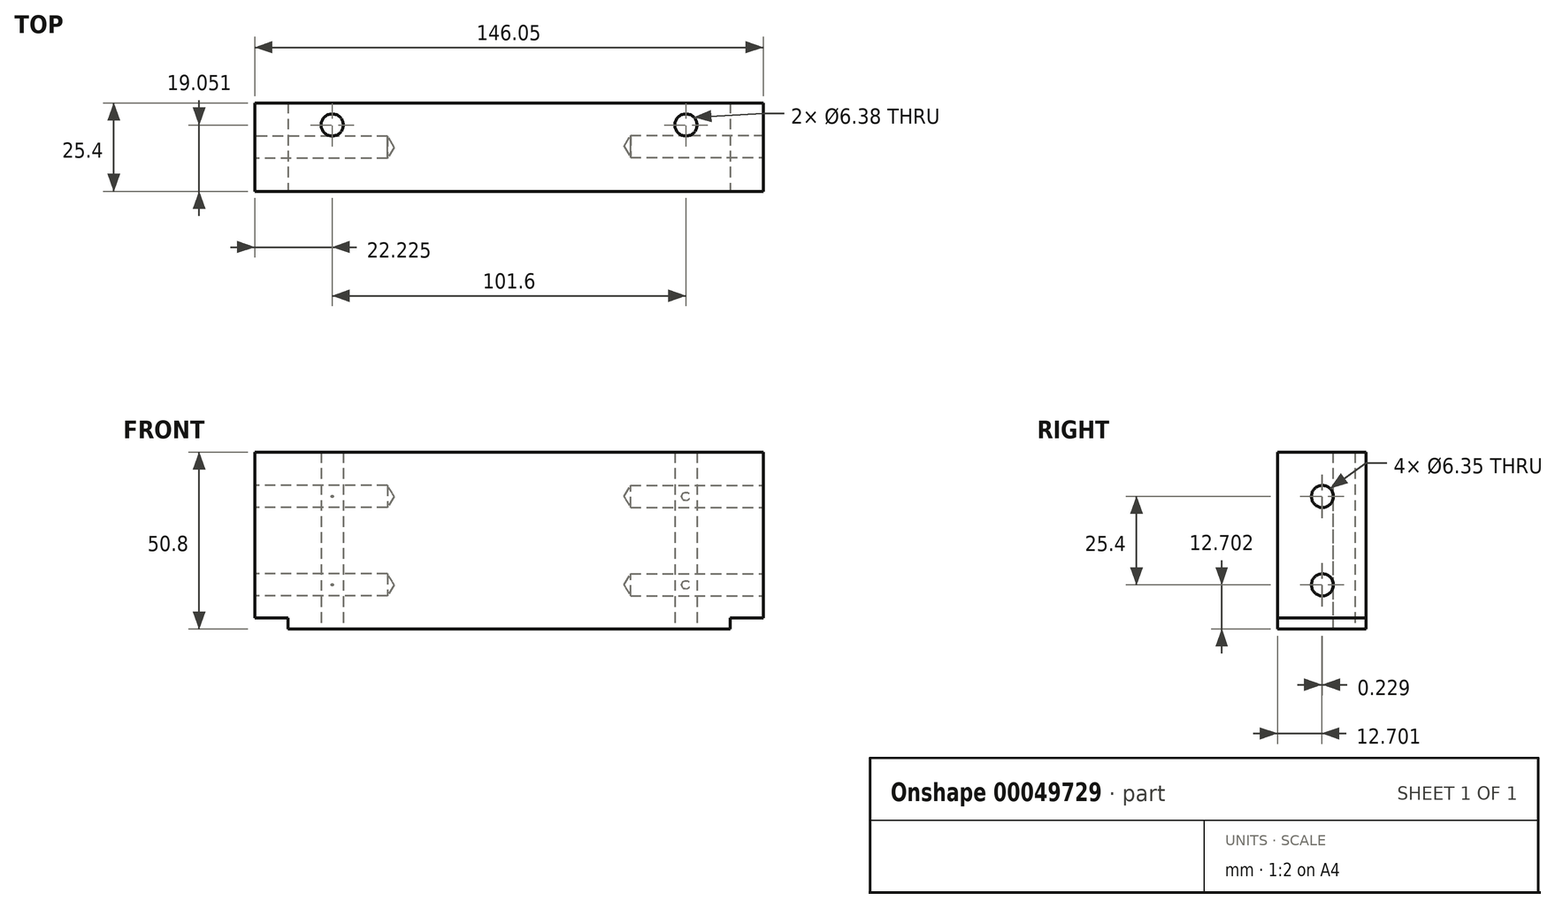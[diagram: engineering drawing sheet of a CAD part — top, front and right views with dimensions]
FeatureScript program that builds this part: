
annotation { "Feature Type Name" : "Feature", "Feature Type Description" : "" }
export const myFeature = defineFeature(function(context is Context, id is Id, definition is map)
    precondition{}
    {
        {
            var Q0;
            Q0=qCreatedBy(makeId("Right.planeOp"),FACE);
            var sketch = newSketch(context, id + "F0", { "sketchPlane" : qUnion([Q0])});
            skLineSegment(sketch, "E0.bottom", {"start": v(-12.93, 36.02) * mm, "end": v(12.47, 36.02) * mm});
            skLineSegment(sketch, "E0.top", {"start": v(-12.93, -14.78) * mm, "end": v(12.47, -14.78) * mm});
            skLineSegment(sketch, "E0.left", {"start": v(-12.93, 36.02) * mm, "end": v(-12.93, -14.78) * mm});
            skLineSegment(sketch, "E0.right", {"start": v(12.47, 36.02) * mm, "end": v(12.47, -14.78) * mm});
            skSolve(sketch);
        }
        {
            var Q0;
            Q0 = qSketchRegion(id + "F0", true);
            extrude(context, id + "F1", {"entities" : qUnion([Q0]), "depth" : 146.05 * mm});
        }
        {
            var Q0;
            Q0=makeQuery(id+"F1.opExtrude","SWEPT_FACE",FACE,{"disambiguationData":[OSD([sQuery(id+"F0.wireOp",EDGE,"E0.top")])]});
            var sketch = newSketch(context, id + "F2", { "sketchPlane" : qUnion([Q0])});
            skLineSegment(sketch, "E1.bottom", {"start": v(146.05, -12.47) * mm, "end": v(136.53, -12.47) * mm});
            skLineSegment(sketch, "E1.top", {"start": v(146.05, 12.93) * mm, "end": v(136.53, 12.93) * mm});
            skLineSegment(sketch, "E1.left", {"start": v(146.05, -12.47) * mm, "end": v(146.05, 12.93) * mm});
            skLineSegment(sketch, "E1.right", {"start": v(136.53, -12.47) * mm, "end": v(136.53, 12.93) * mm});
            skLineSegment(sketch, "E2.bottom", {"start": v(0, -12.47) * mm, "end": v(9.53, -12.47) * mm});
            skLineSegment(sketch, "E2.top", {"start": v(0, 12.93) * mm, "end": v(9.52, 12.93) * mm});
            skLineSegment(sketch, "E2.left", {"start": v(0, -12.47) * mm, "end": v(0, 12.93) * mm});
            skLineSegment(sketch, "E2.right", {"start": v(9.53, -12.47) * mm, "end": v(9.52, 12.93) * mm});
            skSolve(sketch);
        }
        {
            var Q0;
            Q0 = qSketchRegion(id + "F2", true);
            extrude(context, id + "F3", {"entities" : qUnion([Q0]), "operationType" : NewBodyOperationType.REMOVE, "oppositeDirection" : true, "depth" : 3.17 * mm});
        }
        {
            var Q0;
            Q0=makeQuery(id+"F1.opExtrude","CAP_FACE",FACE,{"disambiguationData":[OSD([sQuery(id+"F0.wireOp",EDGE,"E0.bottom"),sQuery(id+"F0.wireOp",EDGE,"E0.top"),sQuery(id+"F0.wireOp",EDGE,"E0.left"),sQuery(id+"F0.wireOp",EDGE,"E0.right")])],"isStart":false});
            var sketch = newSketch(context, id + "F4", { "sketchPlane" : qUnion([Q0])});
            skPoint(sketch, "E3", {"position": v(0, 23.32) * mm});
            skPoint(sketch, "E4", {"position": v(0, -2.08) * mm});
            skSolve(sketch);
        }
        {
            var Q0;
            Q0=sQuery(id+"F4.wireOp",VERTEX,"E3");
            var Q1;
            Q1=sQuery(id+"F4.wireOp",VERTEX,"E4");
            var Q2;
            Q2=makeQuery(id+"F1.opExtrude","SWEPT_BODY",BODY,{"disambiguationData":[OSD([sQuery(id+"F0.wireOp",EDGE,"E0.bottom"),sQuery(id+"F0.wireOp",EDGE,"E0.top"),sQuery(id+"F0.wireOp",EDGE,"E0.left"),sQuery(id+"F0.wireOp",EDGE,"E0.right")])]});
            hole(context, id + "F5", {"style" : HoleStyle.SIMPLE, "holeDiameter" : 6.35 * mm, "endStyle" : HoleEndStyle.BLIND, "holeDepth" : 38.1 * mm, "locations" : qUnion([Q0, Q1]), "scope" : qUnion([Q2])});
        }
        {
            var Q0;
            Q0=makeQuery(id+"F1.opExtrude","CAP_FACE",FACE,{"disambiguationData":[OSD([sQuery(id+"F0.wireOp",EDGE,"E0.bottom"),sQuery(id+"F0.wireOp",EDGE,"E0.top"),sQuery(id+"F0.wireOp",EDGE,"E0.left"),sQuery(id+"F0.wireOp",EDGE,"E0.right")])],"isStart":true});
            var sketch = newSketch(context, id + "F6", { "sketchPlane" : qUnion([Q0])});
            skPoint(sketch, "E5", {"position": v(0.23, 23.32) * mm});
            skPoint(sketch, "E6", {"position": v(0.23, -2.08) * mm});
            skSolve(sketch);
        }
        {
            var Q0;
            Q0=sQuery(id+"F6.wireOp",VERTEX,"E5");
            var Q1;
            Q1=sQuery(id+"F6.wireOp",VERTEX,"E6");
            var Q2;
            Q2=makeQuery(id+"F1.opExtrude","SWEPT_BODY",BODY,{"disambiguationData":[OSD([sQuery(id+"F0.wireOp",EDGE,"E0.bottom"),sQuery(id+"F0.wireOp",EDGE,"E0.top"),sQuery(id+"F0.wireOp",EDGE,"E0.left"),sQuery(id+"F0.wireOp",EDGE,"E0.right")])]});
            hole(context, id + "F7", {"style" : HoleStyle.SIMPLE, "holeDiameter" : 6.35 * mm, "endStyle" : HoleEndStyle.BLIND, "holeDepth" : 38.1 * mm, "locations" : qUnion([Q0, Q1]), "scope" : qUnion([Q2])});
        }
        {
            var Q0;
            Q0=makeQuery(id+"F1.opExtrude","SWEPT_FACE",FACE,{"disambiguationData":[OSD([sQuery(id+"F0.wireOp",EDGE,"E0.top")])]});
            var sketch = newSketch(context, id + "F8", { "sketchPlane" : qUnion([Q0])});
            skPoint(sketch, "E7", {"position": v(123.83, -6.12) * mm});
            skPoint(sketch, "E8", {"position": v(22.23, -6.12) * mm});
            skSolve(sketch);
        }
        {
            var Q0;
            Q0=sQuery(id+"F8.wireOp",VERTEX,"E7");
            var Q1;
            Q1=sQuery(id+"F8.wireOp",VERTEX,"E8");
            var Q2;
            Q2=makeQuery(id+"F1.opExtrude","SWEPT_BODY",BODY,{"disambiguationData":[OSD([sQuery(id+"F0.wireOp",EDGE,"E0.bottom"),sQuery(id+"F0.wireOp",EDGE,"E0.top"),sQuery(id+"F0.wireOp",EDGE,"E0.left"),sQuery(id+"F0.wireOp",EDGE,"E0.right")])]});
            hole(context, id + "F9", {"style" : HoleStyle.SIMPLE, "holeDiameter" : 6.38 * mm, "endStyle" : HoleEndStyle.THROUGH, "locations" : qUnion([Q0, Q1]), "scope" : qUnion([Q2])});
        }
    });
